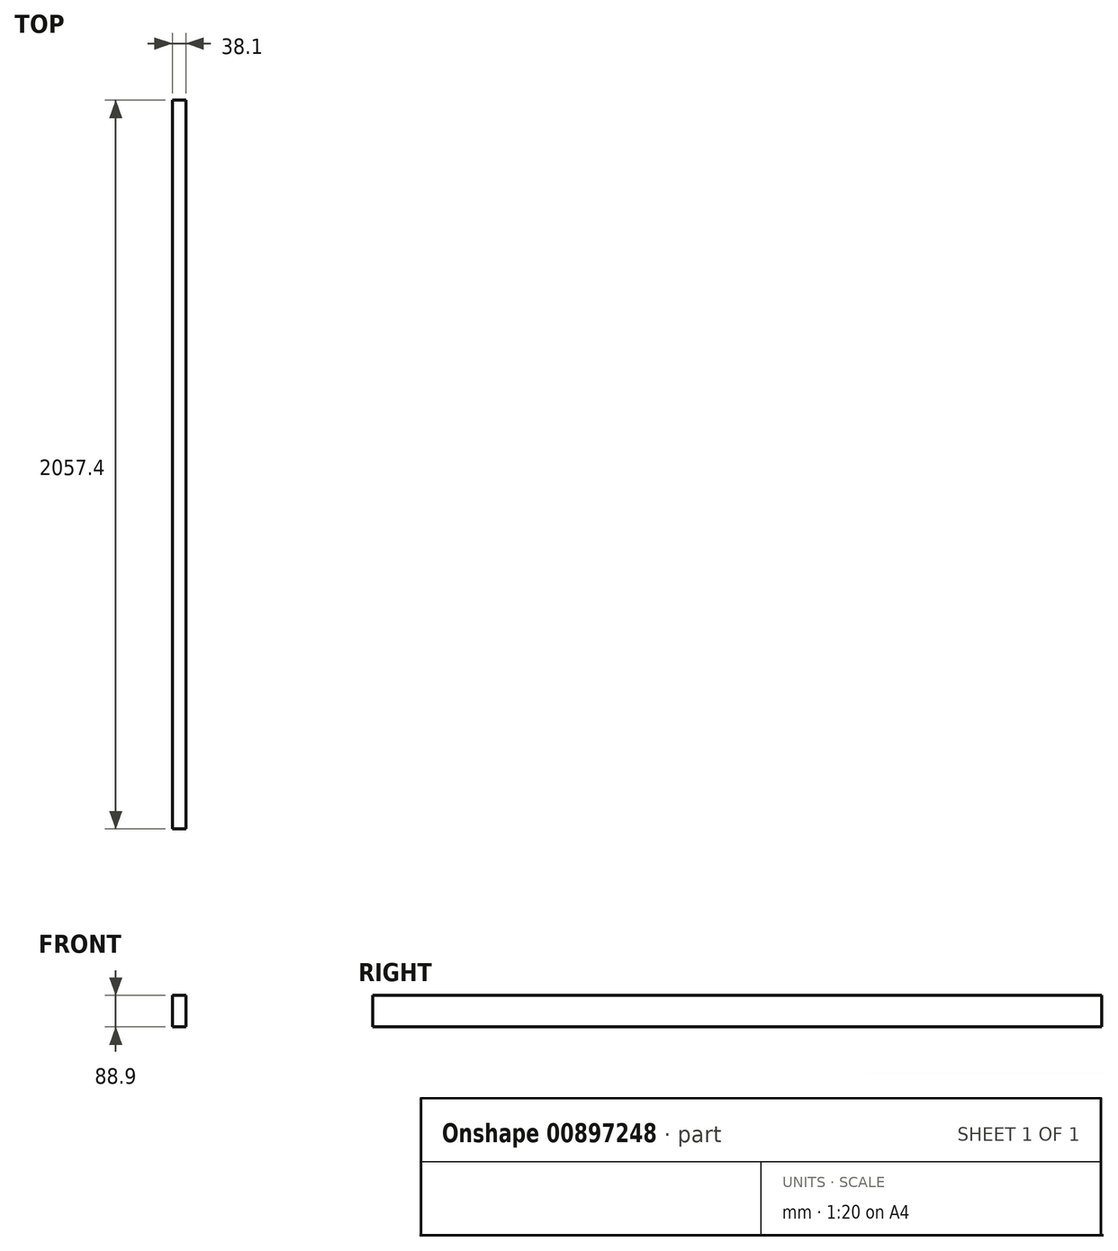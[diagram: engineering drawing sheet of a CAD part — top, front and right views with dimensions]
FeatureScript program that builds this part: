
annotation { "Feature Type Name" : "Feature", "Feature Type Description" : "" }
export const myFeature = defineFeature(function(context is Context, id is Id, definition is map)
    precondition{}
    {
        {
            var Q0;
            Q0=qCreatedBy(makeId("Front.planeOp"),FACE);
            var sketch = newSketch(context, id + "F0", { "sketchPlane" : qUnion([Q0])});
            skLineSegment(sketch, "E0.bottom", {"start": v(-19.05, 44.45) * mm, "end": v(19.05, 44.45) * mm});
            skLineSegment(sketch, "E0.top", {"start": v(-19.05, -44.45) * mm, "end": v(19.05, -44.45) * mm});
            skLineSegment(sketch, "E0.left", {"start": v(-19.05, 44.45) * mm, "end": v(-19.05, -44.45) * mm});
            skLineSegment(sketch, "E0.right", {"start": v(19.05, 44.45) * mm, "end": v(19.05, -44.45) * mm});
            skPoint(sketch, "E0.middle", {"position": v(0, 0) * mm});
            skSolve(sketch);
        }
        {
            var Q0;
            Q0=makeQuery(id+"F0.imprint","IMPRINT",FACE,{"disambiguationData":[TD([[makeQuery(id+"F0.imprint","IMPRINT",EDGE,{"derivedFrom":sQuery(id+"F0.wireOp",EDGE,"E0.bottom")}),-1.0]])]});
            extrude(context, id + "F1", {"entities" : qUnion([Q0]), "depth" : 2057.4 * mm, "offsetDistance" : 25.4 * mm});
        }
    });
